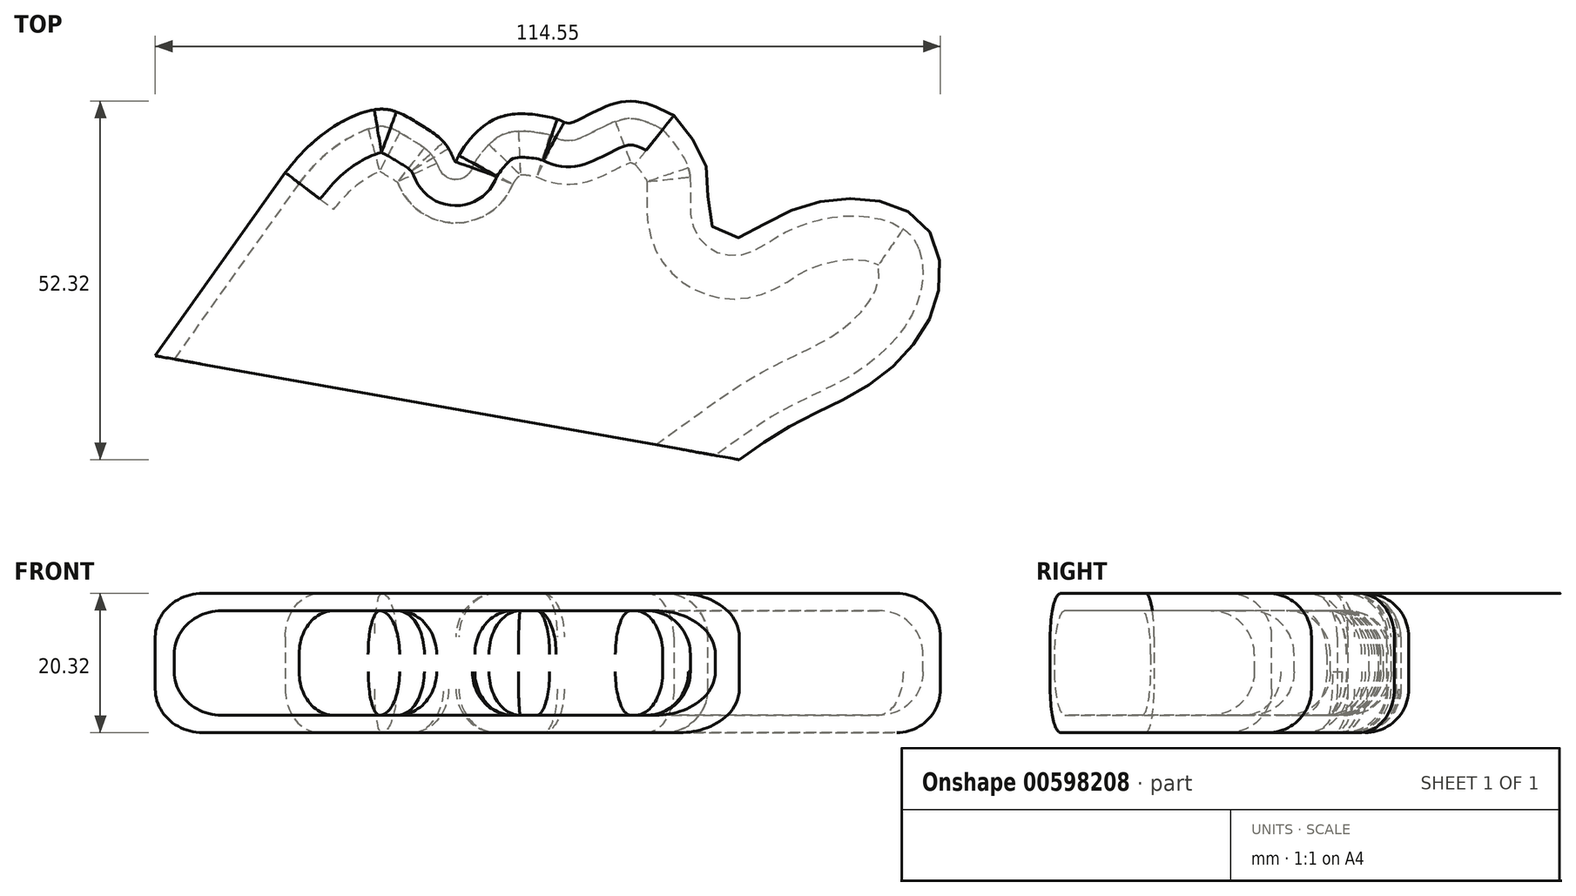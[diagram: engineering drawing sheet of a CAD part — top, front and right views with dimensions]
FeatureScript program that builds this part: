
annotation { "Feature Type Name" : "Feature", "Feature Type Description" : "" }
export const myFeature = defineFeature(function(context is Context, id is Id, definition is map)
    precondition{}
    {
        {
            var Q0;
            Q0=qCreatedBy(makeId("Top.planeOp"),FACE);
            var sketch = newSketch(context, id + "F0", { "sketchPlane" : qUnion([Q0])});
            skLineSegment(sketch, "E0", {"start": v(-2.53, 3.76) * mm, "end": v(-21.5, -22.97) * mm});
            skLineSegment(sketch, "E1", {"start": v(-21.5, -22.97) * mm, "end": v(63.73, -38.13) * mm});
            skFitSpline(sketch, "E2", {"points": [v(54.17, 12.07) * mm, v(59, 4.04) * mm, v(59.53, -3.66) * mm, v(63.11, -5.79) * mm, v(68.43, -3.13) * mm, v(80.08, 0) * mm, v(90.97, -4.14) * mm, v(92.29, -15.51) * mm, v(83.28, -26.78) * mm, v(72.06, -32.72) * mm, v(63.73, -38.13) * mm], "startDerivative": vector(65.3, -76.98) * mm, "endDerivative": vector(-77.9, -55.9) * mm});
            skFitSpline(sketch, "E3", {"points": [v(54.17, 12.07) * mm, v(46.53, 14.07) * mm, v(38.95, 10.97) * mm, v(37.74, 11.32) * mm, v(32.97, 12.3) * mm, v(26.72, 10.78) * mm, v(22.54, 5.75) * mm, v(22.31, 5.3) * mm, v(21.06, 7.64) * mm, v(16.58, 11.13) * mm, v(11.4, 13.03) * mm, v(2.8, 9.24) * mm, v(-2.53, 3.76) * mm], "startDerivative": vector(-69.1, 36.11) * mm, "endDerivative": vector(-44.65, -54.63) * mm});
            skSolve(sketch);
        }
        {
            var Q0;
            Q0=makeQuery(id+"F0.imprint","IMPRINT",FACE,{"disambiguationData":[TD([[makeQuery(id+"F0.imprint","IMPRINT",EDGE,{"derivedFrom":sQuery(id+"F0.wireOp",EDGE,"E0")}),1.0]])]});
            extrude(context, id + "F1", {"entities" : qUnion([Q0]), "depth" : 20.32 * mm, "offsetDistance" : 25.4 * mm});
        }
        {
            var Q0;
            Q0=makeQuery(id+"F1.opExtrude","SWEPT_FACE",FACE,{"disambiguationData":[OSD([sQuery(id+"F0.wireOp",EDGE,"E1")])]});
            shell(context, id + "F2", {"entities" : qUnion([Q0]), "thickness" : 2.54 * mm});
        }
        {
            var Q0;
            {var subQ0=sQuery(id+"F0.wireOp",EDGE,"E3");Q0=makeQuery(id+"F2.opShell","OFFSET_EDGE",EDGE,{"disambiguationData":[OSD([subQ0]),TDD([makeQuery(id+"F1.opExtrude","CAP_EDGE",EDGE,{"disambiguationData":[OSD([subQ0])],"isStart":false})])]});}
            var Q1;
            {var subQ0=sQuery(id+"F0.wireOp",EDGE,"E3");Q1=makeQuery(id+"F2.opShell","OFFSET_EDGE",EDGE,{"disambiguationData":[OSD([subQ0]),TDD([makeQuery(id+"F1.opExtrude","CAP_EDGE",EDGE,{"disambiguationData":[OSD([subQ0])],"isStart":true})])]});}
            var Q2;
            {var subQ0=sQuery(id+"F0.wireOp",EDGE,"E2");Q2=makeQuery(id+"F2.opShell","OFFSET_EDGE",EDGE,{"disambiguationData":[OSD([subQ0]),TDD([makeQuery(id+"F1.opExtrude","CAP_EDGE",EDGE,{"disambiguationData":[OSD([subQ0])],"isStart":true})])]});}
            var Q3;
            {var subQ0=sQuery(id+"F0.wireOp",EDGE,"E2");Q3=makeQuery(id+"F2.opShell","OFFSET_EDGE",EDGE,{"disambiguationData":[OSD([subQ0]),TDD([makeQuery(id+"F1.opExtrude","CAP_EDGE",EDGE,{"disambiguationData":[OSD([subQ0])],"isStart":false})])]});}
            var Q4;
            {var subQ0=sQuery(id+"F0.wireOp",EDGE,"E0");Q4=makeQuery(id+"F2.opShell","OFFSET_EDGE",EDGE,{"disambiguationData":[OSD([subQ0]),TDD([makeQuery(id+"F1.opExtrude","CAP_EDGE",EDGE,{"disambiguationData":[OSD([subQ0])],"isStart":false})])]});}
            var Q5;
            {var subQ0=sQuery(id+"F0.wireOp",EDGE,"E0");Q5=makeQuery(id+"F2.opShell","OFFSET_EDGE",EDGE,{"disambiguationData":[OSD([subQ0]),TDD([makeQuery(id+"F1.opExtrude","CAP_EDGE",EDGE,{"disambiguationData":[OSD([subQ0])],"isStart":true})])]});}
            var Q6;
            Q6=makeQuery(id+"F1.opExtrude","CAP_EDGE",EDGE,{"disambiguationData":[OSD([sQuery(id+"F0.wireOp",EDGE,"E0")])],"isStart":false});
            var Q7;
            Q7=makeQuery(id+"F1.opExtrude","CAP_EDGE",EDGE,{"disambiguationData":[OSD([sQuery(id+"F0.wireOp",EDGE,"E3")])],"isStart":false});
            var Q8;
            Q8=makeQuery(id+"F1.opExtrude","CAP_EDGE",EDGE,{"disambiguationData":[OSD([sQuery(id+"F0.wireOp",EDGE,"E2")])],"isStart":false});
            var Q9;
            Q9=makeQuery(id+"F1.opExtrude","CAP_EDGE",EDGE,{"disambiguationData":[OSD([sQuery(id+"F0.wireOp",EDGE,"E0")])],"isStart":true});
            var Q10;
            Q10=makeQuery(id+"F1.opExtrude","CAP_EDGE",EDGE,{"disambiguationData":[OSD([sQuery(id+"F0.wireOp",EDGE,"E3")])],"isStart":true});
            var Q11;
            Q11=makeQuery(id+"F1.opExtrude","CAP_EDGE",EDGE,{"disambiguationData":[OSD([sQuery(id+"F0.wireOp",EDGE,"E2")])],"isStart":true});
            fillet(context, id + "F3", {"entities" : qUnion([Q0, Q1, Q2, Q3, Q4, Q5, Q6, Q7, Q8, Q9, Q10, Q11]), "radius" : 6.35 * mm, "tangentPropagation" : true, "allowEdgeOverflow" : false});
        }
    });
